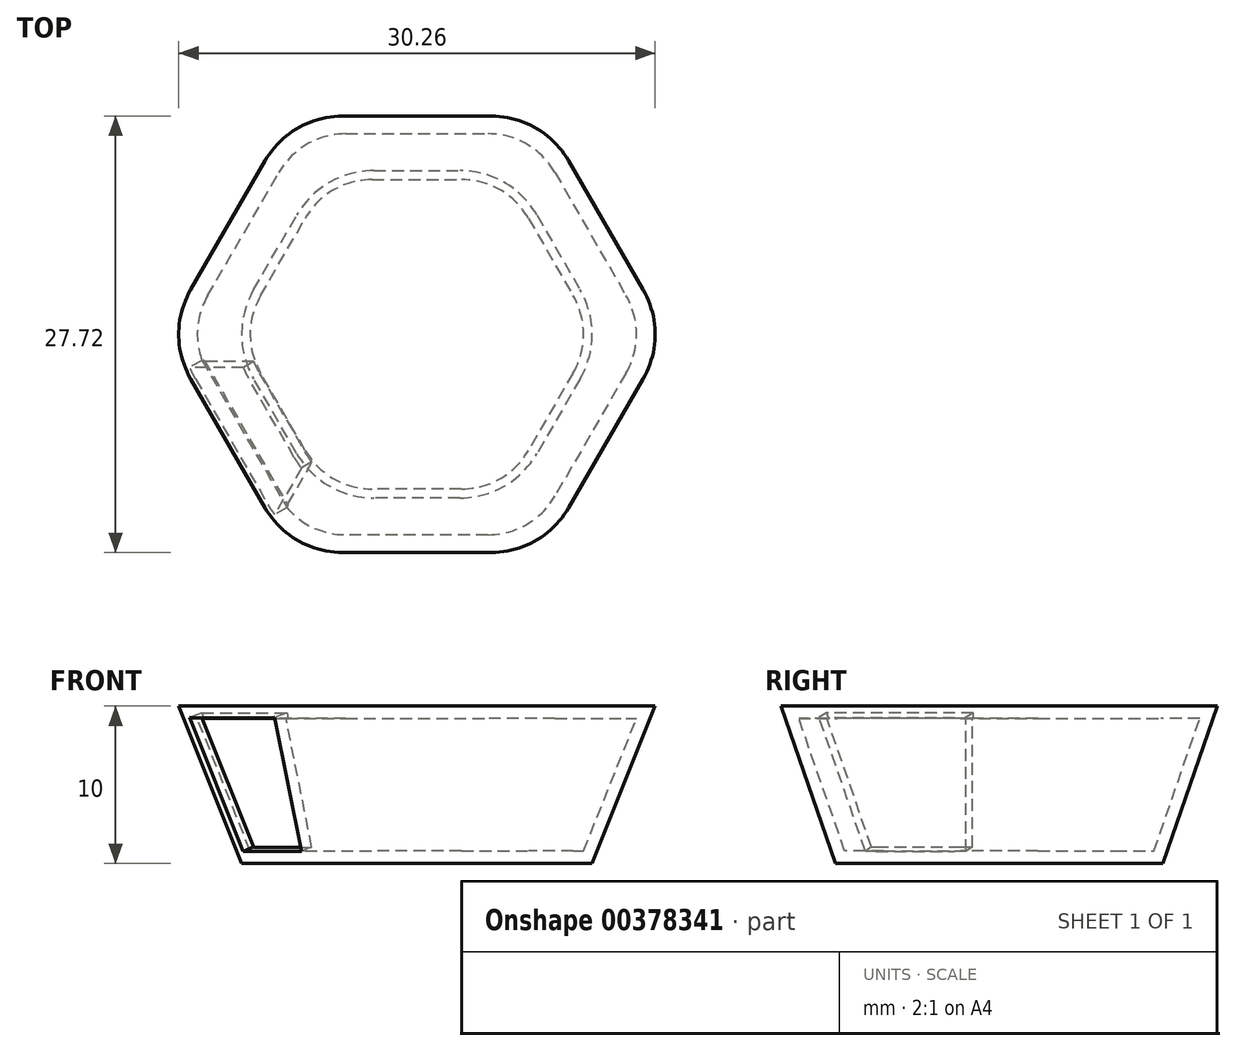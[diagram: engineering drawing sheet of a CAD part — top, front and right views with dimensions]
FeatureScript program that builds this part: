
annotation { "Feature Type Name" : "Feature", "Feature Type Description" : "" }
export const myFeature = defineFeature(function(context is Context, id is Id, definition is map)
    precondition{}
    {
        {
            var Q0;
            Q0=qCreatedBy(makeId("Top.planeOp"),FACE);
            var sketch = newSketch(context, id + "F0", { "sketchPlane" : qUnion([Q0])});
            skCircle(sketch, "E0.cCircle", {"center": v(0, 0) * mm, "radius": 12 * mm, "construction": true});
            skLineSegment(sketch, "E0.0", {"start": v(12, 0) * mm, "end": v(6, -10.4) * mm});
            skLineSegment(sketch, "E0.1", {"start": v(6, -10.4) * mm, "end": v(-6, -10.4) * mm});
            skLineSegment(sketch, "E0.2", {"start": v(-6, -10.4) * mm, "end": v(-12, 0) * mm});
            skLineSegment(sketch, "E0.3", {"start": v(-12, 0) * mm, "end": v(-6, 10.4) * mm});
            skLineSegment(sketch, "E0.4", {"start": v(-6, 10.4) * mm, "end": v(6, 10.4) * mm});
            skLineSegment(sketch, "E0.5", {"start": v(6, 10.4) * mm, "end": v(12, 0) * mm});
            skSolve(sketch);
        }
        {
            var Q0;
            Q0=qCreatedBy(makeId("Top.planeOp"),FACE);
            cPlane(context, id + "F1", {"entities" : qUnion([Q0]), "cplaneType" : CPlaneType.OFFSET, "offset" : 10 * mm, "width" : 150 * mm, "height" : 150 * mm});
        }
        {
            var Q0;
            Q0=qCreatedBy(id+"F1.planeOp",FACE);
            var sketch = newSketch(context, id + "F2", { "sketchPlane" : qUnion([Q0])});
            skCircle(sketch, "E1.cCircle", {"center": v(0, 0) * mm, "radius": 16 * mm, "construction": true});
            skLineSegment(sketch, "E1.0", {"start": v(16, 0) * mm, "end": v(8, -13.86) * mm});
            skLineSegment(sketch, "E1.1", {"start": v(8, -13.86) * mm, "end": v(-8, -13.86) * mm});
            skLineSegment(sketch, "E1.2", {"start": v(-8, -13.86) * mm, "end": v(-16, 0) * mm});
            skLineSegment(sketch, "E1.3", {"start": v(-16, 0) * mm, "end": v(-8, 13.86) * mm});
            skLineSegment(sketch, "E1.4", {"start": v(-8, 13.86) * mm, "end": v(8, 13.86) * mm});
            skLineSegment(sketch, "E1.5", {"start": v(8, 13.86) * mm, "end": v(16, 0) * mm});
            skSolve(sketch);
        }
        {
            var Q0;
            Q0=makeQuery(id+"F0.imprint","IMPRINT",FACE,{"disambiguationData":[TD([[makeQuery(id+"F0.imprint","IMPRINT",EDGE,{"derivedFrom":sQuery(id+"F0.wireOp",EDGE,"E0.0")}),-1.0]])]});
            var Q1;
            Q1=makeQuery(id+"F2.imprint","IMPRINT",FACE,{"disambiguationData":[TD([[makeQuery(id+"F2.imprint","IMPRINT",EDGE,{"derivedFrom":sQuery(id+"F2.wireOp",EDGE,"E1.0")}),-1.0]])]});
            loft(context, id + "F3", {"sheetProfilesArray" : [{ "sheetProfileEntities" : qUnion([Q0]) }, { "sheetProfileEntities" : qUnion([Q1]) }]});
        }
        {
            var Q0;
            Q0=makeQuery(id+"F3.opLoft","SWEPT_EDGE",EDGE,{"disambiguationData":[OSD([sQuery(id+"F0.wireOp",EDGE,"E0.2"),sQuery(id+"F0.wireOp",EDGE,"E0.3"),sQuery(id+"F2.wireOp",EDGE,"E1.2"),sQuery(id+"F2.wireOp",EDGE,"E1.3")])]});
            var Q1;
            Q1=makeQuery(id+"F3.opLoft","SWEPT_EDGE",EDGE,{"disambiguationData":[OSD([sQuery(id+"F0.wireOp",EDGE,"E0.3"),sQuery(id+"F0.wireOp",EDGE,"E0.4"),sQuery(id+"F2.wireOp",EDGE,"E1.3"),sQuery(id+"F2.wireOp",EDGE,"E1.4")])]});
            var Q2;
            Q2=makeQuery(id+"F3.opLoft","SWEPT_EDGE",EDGE,{"disambiguationData":[OSD([sQuery(id+"F0.wireOp",EDGE,"E0.4"),sQuery(id+"F0.wireOp",EDGE,"E0.5"),sQuery(id+"F2.wireOp",EDGE,"E1.4"),sQuery(id+"F2.wireOp",EDGE,"E1.5")])]});
            var Q3;
            Q3=makeQuery(id+"F3.opLoft","SWEPT_EDGE",EDGE,{"disambiguationData":[OSD([sQuery(id+"F0.wireOp",EDGE,"E0.0"),sQuery(id+"F0.wireOp",EDGE,"E0.5"),sQuery(id+"F2.wireOp",EDGE,"E1.0"),sQuery(id+"F2.wireOp",EDGE,"E1.5")])]});
            var Q4;
            Q4=makeQuery(id+"F3.opLoft","SWEPT_EDGE",EDGE,{"disambiguationData":[OSD([sQuery(id+"F0.wireOp",EDGE,"E0.0"),sQuery(id+"F0.wireOp",EDGE,"E0.1"),sQuery(id+"F2.wireOp",EDGE,"E1.0"),sQuery(id+"F2.wireOp",EDGE,"E1.1")])]});
            var Q5;
            Q5=makeQuery(id+"F3.opLoft","SWEPT_EDGE",EDGE,{"disambiguationData":[OSD([sQuery(id+"F0.wireOp",EDGE,"E0.1"),sQuery(id+"F0.wireOp",EDGE,"E0.2"),sQuery(id+"F2.wireOp",EDGE,"E1.1"),sQuery(id+"F2.wireOp",EDGE,"E1.2")])]});
            fillet(context, id + "F4", {"entities" : qUnion([Q0, Q1, Q2, Q3, Q4, Q5]), "radius" : 6 * mm, "tangentPropagation" : true, "allowEdgeOverflow" : false});
        }
        {
            var Q0;
            Q0=makeQuery(id+"F3.opLoft","SWEPT_FACE",FACE,{"disambiguationData":[OSD([sQuery(id+"F0.wireOp",EDGE,"E0.1"),sQuery(id+"F0.wireOp",EDGE,"E0.2"),sQuery(id+"F0.wireOp",EDGE,"E0.3"),sQuery(id+"F2.wireOp",EDGE,"E1.1"),sQuery(id+"F2.wireOp",EDGE,"E1.2"),sQuery(id+"F2.wireOp",EDGE,"E1.3")])]});
            var Q1;
            Q1=makeQuery(id+"F3.opLoft","SWEPT_BODY",BODY,{"disambiguationData":[OSD([makeQuery(id+"F0.imprint","IMPRINT",FACE,{"disambiguationData":[TD([[makeQuery(id+"F0.imprint","IMPRINT",EDGE,{"derivedFrom":sQuery(id+"F0.wireOp",EDGE,"E0.0")}),-1.0]])]}),makeQuery(id+"F2.imprint","IMPRINT",FACE,{"disambiguationData":[TD([[makeQuery(id+"F2.imprint","IMPRINT",EDGE,{"derivedFrom":sQuery(id+"F2.wireOp",EDGE,"E1.0")}),-1.0]])]})])]});
            shell(context, id + "F5", {"isHollow" : true, "entities" : qUnion([Q0]), "parts" : qUnion([Q1]), "thickness" : 0.8 * mm});
        }
        {
            var Q0;
            Q0=makeQuery(id+"F3.opLoft","SWEPT_FACE",FACE,{"disambiguationData":[OSD([sQuery(id+"F0.wireOp",EDGE,"E0.1"),sQuery(id+"F0.wireOp",EDGE,"E0.2"),sQuery(id+"F0.wireOp",EDGE,"E0.3"),sQuery(id+"F2.wireOp",EDGE,"E1.1"),sQuery(id+"F2.wireOp",EDGE,"E1.2"),sQuery(id+"F2.wireOp",EDGE,"E1.3")])]});
            var sketch = newSketch(context, id + "F6", { "sketchPlane" : qUnion([Q0])});
            skLineSegment(sketch, "E2", {"start": v(-2.85, 13.96) * mm, "end": v(7.74, 11.95) * mm});
            skLineSegment(sketch, "E3", {"start": v(7.74, 11.95) * mm, "end": v(4.4, 3.44) * mm});
            skLineSegment(sketch, "E4", {"start": v(4.4, 3.44) * mm, "end": v(-2.85, 4.81) * mm});
            skLineSegment(sketch, "E5", {"start": v(-2.85, 4.81) * mm, "end": v(-2.85, 13.96) * mm});
            skLineSegment(sketch, "E6", {"start": v(-2.85, 13.96) * mm, "end": v(-2.85, 13.96) * mm});
            skSolve(sketch);
        }
        {
            var Q0;
            Q0 = qSketchRegion(id + "F6", true);
            extrude(context, id + "F7", {"entities" : qUnion([Q0]), "operationType" : NewBodyOperationType.REMOVE, "oppositeDirection" : true, "depth" : 1 * mm});
        }
    });
